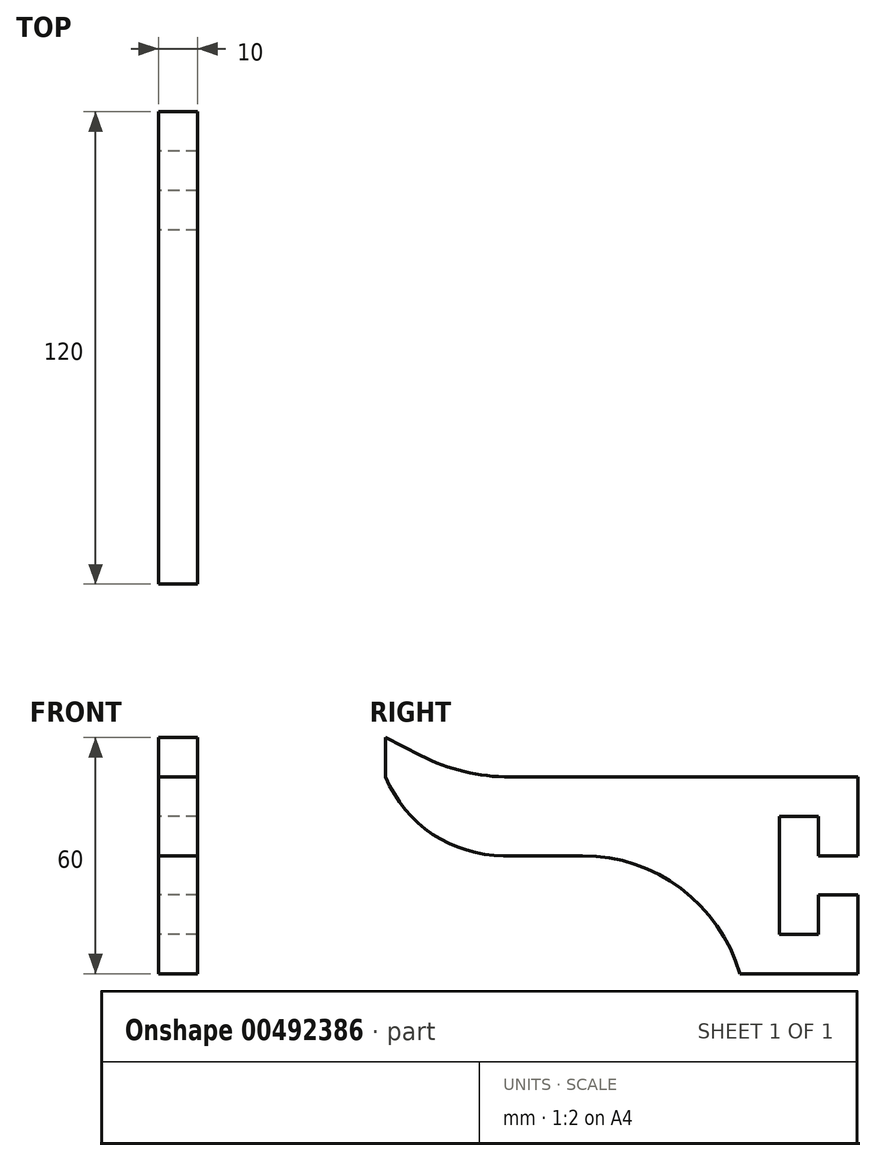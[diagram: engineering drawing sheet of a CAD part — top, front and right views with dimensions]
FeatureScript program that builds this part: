
annotation { "Feature Type Name" : "Feature", "Feature Type Description" : "" }
export const myFeature = defineFeature(function(context is Context, id is Id, definition is map)
    precondition{}
    {
        {
            var Q0;
            Q0=qCreatedBy(makeId("Right.planeOp"),FACE);
            var sketch = newSketch(context, id + "F0", { "sketchPlane" : qUnion([Q0])});
            skLineSegment(sketch, "E0", {"start": v(-30, 30) * mm, "end": v(-21.1, 25.46) * mm});
            skLineSegment(sketch, "E1", {"start": v(1.62, 20) * mm, "end": v(70, 20) * mm});
            skLineSegment(sketch, "E2", {"start": v(70, 20) * mm, "end": v(70, -30) * mm});
            skLineSegment(sketch, "E3", {"start": v(70, -30) * mm, "end": v(60, -30) * mm});
            skLineSegment(sketch, "E4", {"start": v(-30, 20) * mm, "end": v(-30, 30) * mm});
            skPoint(sketch, "E5.visualSharp", {"position": v(-10.39, 20) * mm});
            skArc(sketch, "E5.filletArc", {"start": v(-21.1, 25.46) * mm, "mid": v(-10.06, 21.38) * mm, "end": v(1.62, 20) * mm});
            skArc(sketch, "E6", {"start": v(-30, 20) * mm, "mid": v(-18.03, 5.46) * mm, "end": v(0, 0) * mm});
            skLineSegment(sketch, "E7", {"start": v(0, 0) * mm, "end": v(20, 0) * mm});
            skArc(sketch, "E8", {"start": v(60, -30) * mm, "mid": v(45, -8.33) * mm, "end": v(20, 0) * mm});
            skLineSegment(sketch, "E9", {"start": v(70, 20) * mm, "end": v(90, 20) * mm});
            skLineSegment(sketch, "E10", {"start": v(90, 20) * mm, "end": v(90, 0) * mm});
            skLineSegment(sketch, "E11", {"start": v(90, 0) * mm, "end": v(80, 0) * mm});
            skLineSegment(sketch, "E12", {"start": v(80, 0) * mm, "end": v(80, 10) * mm});
            skLineSegment(sketch, "E13", {"start": v(80, 10) * mm, "end": v(70, 10) * mm});
            skLineSegment(sketch, "E14", {"start": v(70, -30) * mm, "end": v(90, -30) * mm});
            skLineSegment(sketch, "E15", {"start": v(90, -30) * mm, "end": v(90, -10) * mm});
            skLineSegment(sketch, "E16", {"start": v(90, -10) * mm, "end": v(80, -10) * mm});
            skLineSegment(sketch, "E17", {"start": v(80, -10) * mm, "end": v(80, -20) * mm});
            skLineSegment(sketch, "E18", {"start": v(80, -20) * mm, "end": v(70, -20) * mm});
            skSolve(sketch);
        }
        {
            var Q0;
            Q0 = qSketchRegion(id + "F0", true);
            extrude(context, id + "F1", {"entities" : qUnion([Q0]), "depth" : 10 * mm});
        }
    });
